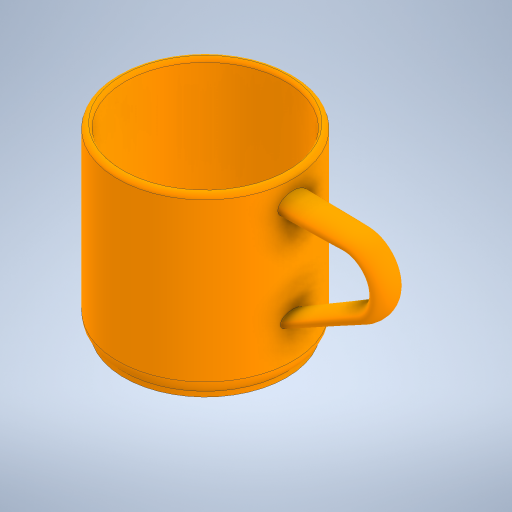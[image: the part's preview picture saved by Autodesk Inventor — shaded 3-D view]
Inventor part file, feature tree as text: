
AUTODESK INVENTOR PART (.ipt)
format: ipt  version: 2024.2 (Build 282272000, 272)  size: 366,080 bytes
history: native  units: in
note: dims shown in document units (in); Inventor stores cm internally (conversion verified against a paired STEP export)
features: sketch x6, other x1, revolve x1, shell x1, plane x1, loft x1, fillet x1, extrude x1
ambient origin geometry x8: Origin, YZ Plane, XZ Plane, XY Plane, X Axis, Y Axis, Z Axis, Center Point
bodies: Solid1 (feature_tree)
feature tree (13):
  other  "CrossSection1"
  revolve  "Revolution1"  [1 undecoded]
  shell  "Shell1"  Thickness=2.5591in
  sketch  "Sketch2"  dims[d3=1.2795in d4=90.0deg d5=0.1181in]
  sketch  "Sketch3"  dims[d6=0.0197in d7=0.0787in d8=0.0in d9=0.7874in d26=0.0in d27=90.0deg]
  plane  "Work Plane3"
  loft  "Loft1"
  fillet  "Fillet1"  Radius=0.1181in
  extrude  "Extrusion1"  TaperAngle=0.0deg  [1 undecoded]
  sketch  "Sketch1"  dims[d0=2.7559in d1=1.378in d2=2.5591in]
  sketch  "Sketch4"  dims[d28=0.0in d29=90.0deg]
  sketch  "Sketch5"  dims[d30=0.0in d31=90.0deg]
  sketch  "Sketch6"  dims[d32=0.0787in d33=2.5591in d34=2.4409in d35=0.0787in d36=0.0in]
note: 2 required parameter values undecoded (feature->parameter linkage not recoverable at this tier; creation-order binding heuristic only, values carry confidence <= 0.55)